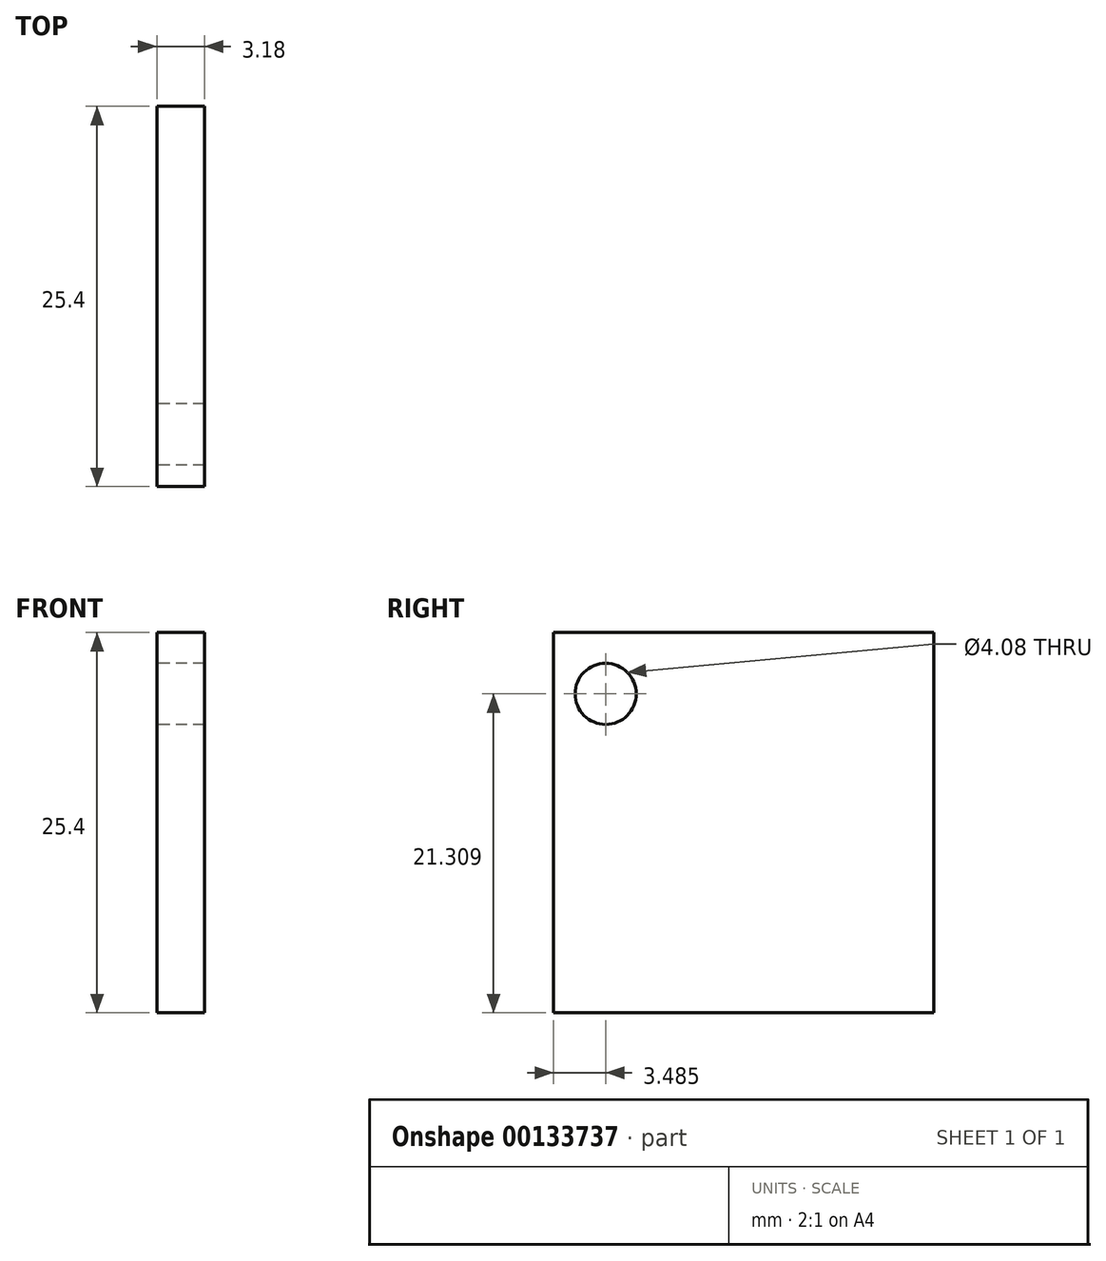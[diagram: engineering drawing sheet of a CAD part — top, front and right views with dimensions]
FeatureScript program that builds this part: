
annotation { "Feature Type Name" : "Feature", "Feature Type Description" : "" }
export const myFeature = defineFeature(function(context is Context, id is Id, definition is map)
    precondition{}
    {
        {
            var Q0;
            Q0=qCreatedBy(makeId("Right.planeOp"),FACE);
            var sketch = newSketch(context, id + "F0", { "sketchPlane" : qUnion([Q0])});
            skLineSegment(sketch, "E0.bottom", {"start": v(0, 0) * mm, "end": v(25.4, 0) * mm});
            skLineSegment(sketch, "E0.top", {"start": v(0, 25.4) * mm, "end": v(25.4, 25.4) * mm});
            skLineSegment(sketch, "E0.left", {"start": v(0, 0) * mm, "end": v(0, 25.4) * mm});
            skLineSegment(sketch, "E0.right", {"start": v(25.4, 0) * mm, "end": v(25.4, 25.4) * mm});
            skCircle(sketch, "E1", {"center": v(3.48, 21.3) * mm, "radius": 2.04 * mm});
            skSolve(sketch);
        }
        {
            var Q0;
            Q0 = qSketchRegion(id + "F0", true);
            extrude(context, id + "F1", {"entities" : qUnion([Q0]), "depth" : 3.17 * mm});
        }
    });
